# Revit family: Furniture-Wall_Mount-Cabinet-KOHLER-BEAUXLINE-K-33533_1
name_source: partatom
category: Casework
revit_build: Autodesk Revit 2017 (Build: 20160225_1515(x64)
units: mm (PartAtom-declared; Revit-internal decimal feet)

## family parameters
Cut with Voids When Loaded = No
Host = Face
OmniClass Number = 23.21.19.00
OmniClass Title = Casework
Room Calculation Point = No
Shared = No

## types (2) — shared parameters
ADA Compliant = No
Assembly Code = E2010.30
Construction Type = Wall Mount
Date Modified = 02/18/2021
Default Elevation = 36"
Depth = 11"
Description = Wall Cabinet 24 Inches
Hardware Included = Yes
Height = 28"
Manufacturer = KOHLER Co.
Master Format 2014 = 12 35 30.23
Master Format 2014 Name = Bathroom Casework
Material = Solid Wood
Product Documentation Link = https://www.us.kohler.com
Product Name = BEAUXLINE
Product Page URL = http://www.us.kohler.com
URL = https://www.us.kohler.com
WaterSense Certified = No
Width = 24"

## per-type parameters (varying)
| type | Finish | Model | Product Finish | Type |
| 0- White | Kohler-Wood-Molded-0-White | K-33533-ASB-0 | Kohler-Wood-Molded-0-White | 1 |
| 1WX-New Dark Grey | KOHLER-Wood-1WX-New_Dark_Grey | K-33533-ASB-1WX | KOHLER-Wood-1WX-New_Dark_Grey | 2 |

## geometry (parser evidence)
native form markers: Sweep x4
no freeform markers — native parametric forms only
